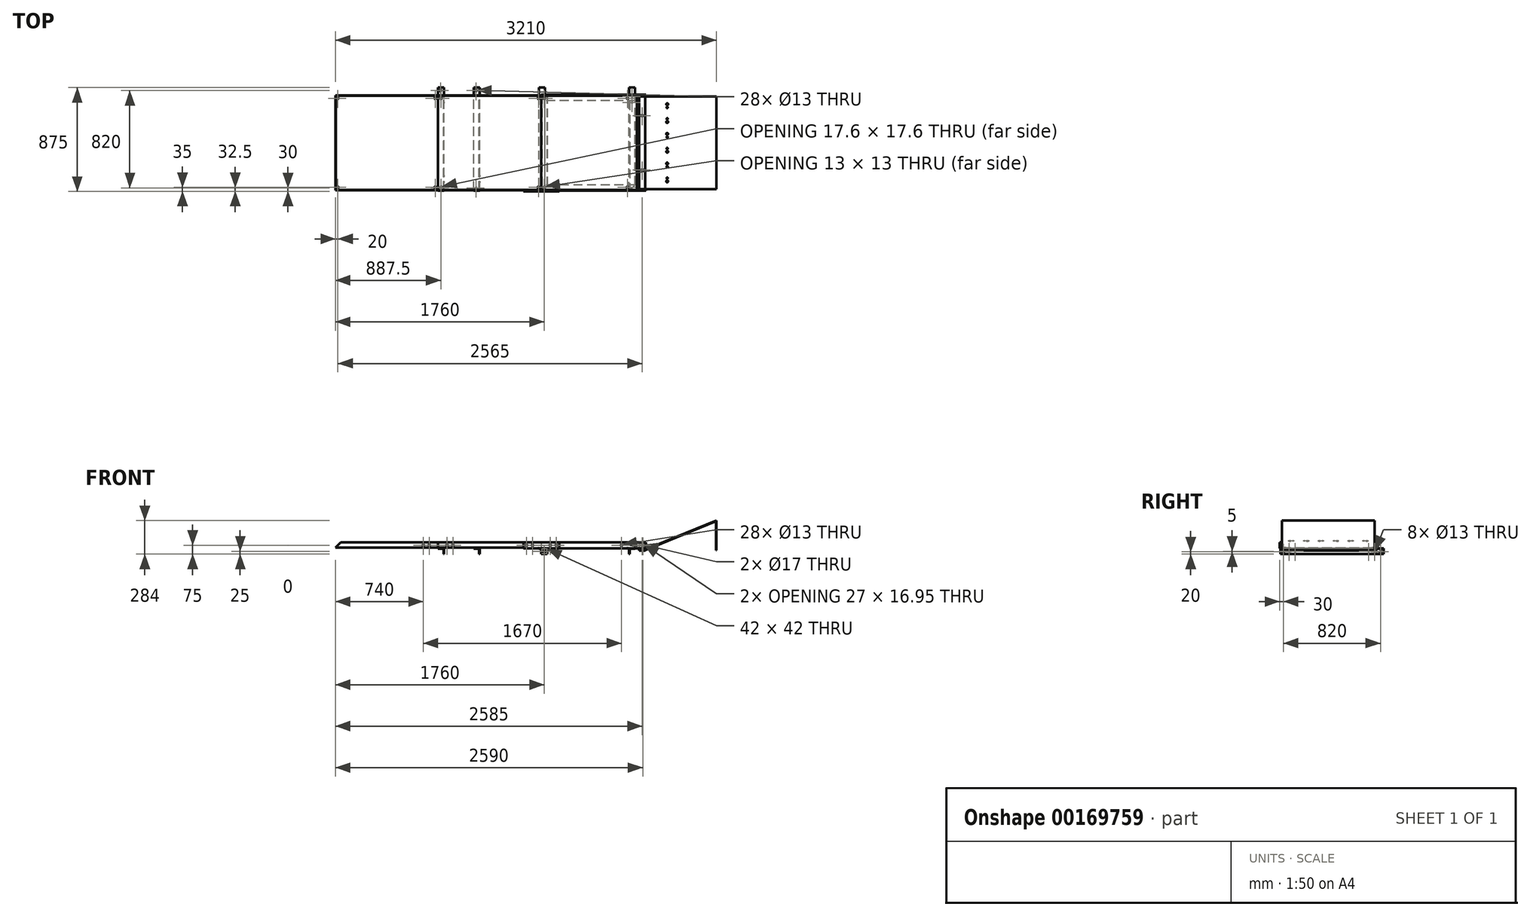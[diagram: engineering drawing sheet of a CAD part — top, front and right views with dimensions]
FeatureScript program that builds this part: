
annotation { "Feature Type Name" : "Feature", "Feature Type Description" : "" }
export const myFeature = defineFeature(function(context is Context, id is Id, definition is map)
    precondition{}
    {
        {
            var Q0;
            Q0=qCreatedBy(makeId("Front.planeOp"),FACE);
            var sketch = newSketch(context, id + "F0", { "sketchPlane" : qUnion([Q0])});
            skLineSegment(sketch, "E0", {"start": v(0, 0) * mm, "end": v(0, 4) * mm});
            skLineSegment(sketch, "E1", {"start": v(0, 4) * mm, "end": v(50, 4) * mm});
            skLineSegment(sketch, "E2", {"start": v(50, 4) * mm, "end": v(650, 250) * mm});
            skLineSegment(sketch, "E3", {"start": v(650, 250) * mm, "end": v(650, 0) * mm});
            skLineSegment(sketch, "E4", {"start": v(650, 0) * mm, "end": v(646, 0) * mm});
            skLineSegment(sketch, "E5", {"start": v(646, 0) * mm, "end": v(646, 244.04) * mm});
            skLineSegment(sketch, "E6", {"start": v(646, 244.04) * mm, "end": v(50.79, 0) * mm});
            skLineSegment(sketch, "E7", {"start": v(50.79, 0) * mm, "end": v(0, 0) * mm});
            skSolve(sketch);
        }
        {
            var Q0;
            Q0=qSketchRegion(id+"F0",true);
            extrude(context, id + "F1", {"entities" : qUnion([Q0]), "oppositeDirection" : true, "depth" : 780 * mm});
        }
        {
            var Q0;
            Q0=qCreatedBy(makeId("Right.planeOp"),FACE);
            var sketch = newSketch(context, id + "F2", { "sketchPlane" : qUnion([Q0])});
            skLineSegment(sketch, "E8", {"start": v(0, 0) * mm, "end": v(-7, 0) * mm});
            skLineSegment(sketch, "E9", {"start": v(-7, 0) * mm, "end": v(-7, 66) * mm});
            skLineSegment(sketch, "E10", {"start": v(-7, 66) * mm, "end": v(-11, 66) * mm});
            skLineSegment(sketch, "E11", {"start": v(-11, 66) * mm, "end": v(-11, -4) * mm});
            skLineSegment(sketch, "E12", {"start": v(-11, -4) * mm, "end": v(791, -4) * mm});
            skLineSegment(sketch, "E13", {"start": v(791, -4) * mm, "end": v(791, 66) * mm});
            skLineSegment(sketch, "E14", {"start": v(791, 66) * mm, "end": v(787, 66) * mm});
            skLineSegment(sketch, "E15", {"start": v(787, 66) * mm, "end": v(787, 0) * mm});
            skLineSegment(sketch, "E16", {"start": v(787, 0) * mm, "end": v(0, 0) * mm});
            skSolve(sketch);
        }
        {
            var Q0;
            Q0=makeQuery(id+"F2.imprint","IMPRINT",FACE,{"disambiguationData":[TD([[makeQuery(id+"F2.imprint","IMPRINT",EDGE,{"derivedFrom":sQuery(id+"F2.wireOp",EDGE,"E8")}),1.0]])]});
            extrude(context, id + "F3", {"entities" : qUnion([Q0]), "depth" : 50 * mm});
        }
        {
            var Q0;
            Q0=makeQuery(id+"F3.opExtrude","SWEPT_FACE",FACE,{"disambiguationData":[OSD([sQuery(id+"F2.wireOp",EDGE,"E11")])]});
            var sketch = newSketch(context, id + "F4", { "sketchPlane" : qUnion([Q0])});
            skCircle(sketch, "E17", {"center": v(20, 41) * mm, "radius": 8.5 * mm});
            skSolve(sketch);
        }
        {
            var Q0;
            Q0=qSketchRegion(id+"F4",true);
            extrude(context, id + "F5", {"entities" : qUnion([Q0]), "operationType" : NewBodyOperationType.REMOVE, "endBound" : BoundingType.THROUGH_ALL, "oppositeDirection" : true, "depth" : 25 * mm});
        }
        {
            var Q0;
            Q0=makeQuery(id+"F3.opExtrude","SWEPT_FACE",FACE,{"disambiguationData":[OSD([sQuery(id+"F2.wireOp",EDGE,"E11")])]});
            var sketch = newSketch(context, id + "F6", { "sketchPlane" : qUnion([Q0])});
            skLineSegment(sketch, "E18.bottom", {"start": v(55, 66) * mm, "end": v(-825, 66) * mm});
            skLineSegment(sketch, "E18.top", {"start": v(55, 16) * mm, "end": v(-825, 16) * mm});
            skLineSegment(sketch, "E18.left", {"start": v(55, 66) * mm, "end": v(55, 16) * mm});
            skLineSegment(sketch, "E18.right", {"start": v(-825, 66) * mm, "end": v(-825, 16) * mm});
            skSolve(sketch);
        }
        {
            var Q0;
            Q0=qSketchRegion(id+"F6",true);
            extrude(context, id + "F7", {"entities" : qUnion([Q0]), "depth" : 4 * mm});
        }
        {
            var Q0;
            Q0=makeQuery(id+"F7.opExtrude","CAP_FACE",FACE,{"disambiguationData":[OSD([sQuery(id+"F6.wireOp",EDGE,"E18.bottom"),sQuery(id+"F6.wireOp",EDGE,"E18.top"),sQuery(id+"F6.wireOp",EDGE,"E18.left"),sQuery(id+"F6.wireOp",EDGE,"E18.right")])],"isStart":true});
            var sketch = newSketch(context, id + "F8", { "sketchPlane" : qUnion([Q0])});
            skLineSegment(sketch, "E19.bottom", {"start": v(20, 16) * mm, "end": v(825, 16) * mm});
            skLineSegment(sketch, "E19.top", {"start": v(20, 20) * mm, "end": v(825, 20) * mm});
            skLineSegment(sketch, "E19.left", {"start": v(20, 16) * mm, "end": v(20, 20) * mm});
            skLineSegment(sketch, "E19.right", {"start": v(825, 16) * mm, "end": v(825, 20) * mm});
            skSolve(sketch);
        }
        {
            var Q0;
            Q0=qSketchRegion(id+"F8",true);
            extrude(context, id + "F9", {"entities" : qUnion([Q0]), "operationType" : NewBodyOperationType.ADD, "depth" : 46 * mm});
        }
        {
            var Q0;
            Q0=makeQuery(id+"F3.opExtrude","SWEPT_FACE",FACE,{"disambiguationData":[OSD([sQuery(id+"F2.wireOp",EDGE,"E13")])]});
            var sketch = newSketch(context, id + "F10", { "sketchPlane" : qUnion([Q0])});
            skLineSegment(sketch, "E20.bottom", {"start": v(-55, 66) * mm, "end": v(825, 66) * mm});
            skLineSegment(sketch, "E20.top", {"start": v(-55, 16) * mm, "end": v(825, 16) * mm});
            skLineSegment(sketch, "E20.left", {"start": v(-55, 66) * mm, "end": v(-55, 16) * mm});
            skLineSegment(sketch, "E20.right", {"start": v(825, 66) * mm, "end": v(825, 16) * mm});
            skSolve(sketch);
        }
        {
            var Q0;
            Q0=qSketchRegion(id+"F10",true);
            extrude(context, id + "F11", {"entities" : qUnion([Q0]), "depth" : 4 * mm});
        }
        {
            var Q0;
            Q0=makeQuery(id+"F11.opExtrude","CAP_FACE",FACE,{"disambiguationData":[OSD([sQuery(id+"F10.wireOp",EDGE,"E20.bottom"),sQuery(id+"F10.wireOp",EDGE,"E20.top"),sQuery(id+"F10.wireOp",EDGE,"E20.left"),sQuery(id+"F10.wireOp",EDGE,"E20.right")])],"isStart":true});
            var sketch = newSketch(context, id + "F12", { "sketchPlane" : qUnion([Q0])});
            skLineSegment(sketch, "E21.bottom", {"start": v(-825, 16) * mm, "end": v(-20, 16) * mm});
            skLineSegment(sketch, "E21.top", {"start": v(-825, 20) * mm, "end": v(-20, 20) * mm});
            skLineSegment(sketch, "E21.left", {"start": v(-825, 16) * mm, "end": v(-825, 20) * mm});
            skLineSegment(sketch, "E21.right", {"start": v(-20, 16) * mm, "end": v(-20, 20) * mm});
            skSolve(sketch);
        }
        {
            var Q0;
            Q0=makeQuery(id+"F12.imprint","IMPRINT",FACE,{"disambiguationData":[TD([[makeQuery(id+"F12.imprint","IMPRINT",EDGE,{"derivedFrom":sQuery(id+"F12.wireOp",EDGE,"E21.bottom")}),-1.0]])]});
            extrude(context, id + "F13", {"entities" : qUnion([Q0]), "operationType" : NewBodyOperationType.ADD, "depth" : 46 * mm});
        }
        {
            var Q0;
            Q0=makeQuery(id+"F9.boolean.opBoolean","MERGE",FACE,{"derivedFrom":[makeQuery(id+"F7.opExtrude","SWEPT_FACE",FACE,{"disambiguationData":[OSD([sQuery(id+"F6.wireOp",EDGE,"E18.top")])]}),makeQuery(id+"F9.opExtrude","SWEPT_FACE",FACE,{"disambiguationData":[OSD([sQuery(id+"F8.wireOp",EDGE,"E19.bottom")])]})]});
            var sketch = newSketch(context, id + "F14", { "sketchPlane" : qUnion([Q0])});
            skLineSegment(sketch, "E22.bottom", {"start": v(-845, 15) * mm, "end": v(-795, 15) * mm});
            skLineSegment(sketch, "E22.top", {"start": v(-845, -855) * mm, "end": v(-795, -855) * mm});
            skLineSegment(sketch, "E22.left", {"start": v(-845, 15) * mm, "end": v(-845, -855) * mm});
            skLineSegment(sketch, "E22.right", {"start": v(-795, 15) * mm, "end": v(-795, -855) * mm});
            skLineSegment(sketch, "E23.bottom", {"start": v(-1645, 15) * mm, "end": v(-1695, 15) * mm});
            skLineSegment(sketch, "E23.top", {"start": v(-1645, -855) * mm, "end": v(-1695, -855) * mm});
            skLineSegment(sketch, "E23.left", {"start": v(-1645, 15) * mm, "end": v(-1645, -855) * mm});
            skLineSegment(sketch, "E23.right", {"start": v(-1695, 15) * mm, "end": v(-1695, -855) * mm});
            skLineSegment(sketch, "E24.bottom", {"start": v(-35.12, 15) * mm, "end": v(-85.12, 15) * mm});
            skLineSegment(sketch, "E24.top", {"start": v(-35.12, -855) * mm, "end": v(-85.12, -855) * mm});
            skLineSegment(sketch, "E24.left", {"start": v(-35.12, 15) * mm, "end": v(-35.12, -855) * mm});
            skLineSegment(sketch, "E24.right", {"start": v(-85.12, 15) * mm, "end": v(-85.12, -855) * mm});
            skSolve(sketch);
        }
        {
            var Q0;
            Q0=qSketchRegion(id+"F14",true);
            extrude(context, id + "F15", {"entities" : qUnion([Q0]), "depth" : 4 * mm});
        }
        {
            var Q0;
            Q0=makeQuery(id+"F15.opExtrude","CAP_FACE",FACE,{"disambiguationData":[OSD([sQuery(id+"F14.wireOp",EDGE,"E23.bottom"),sQuery(id+"F14.wireOp",EDGE,"E23.top"),sQuery(id+"F14.wireOp",EDGE,"E23.left"),sQuery(id+"F14.wireOp",EDGE,"E23.right")])],"isStart":false});
            var sketch = newSketch(context, id + "F16", { "sketchPlane" : qUnion([Q0])});
            skLineSegment(sketch, "E25.bottom", {"start": v(-1645, 15) * mm, "end": v(-1649, 15) * mm});
            skLineSegment(sketch, "E25.top", {"start": v(-1645, -855) * mm, "end": v(-1649, -855) * mm});
            skLineSegment(sketch, "E25.left", {"start": v(-1645, 15) * mm, "end": v(-1645, -855) * mm});
            skLineSegment(sketch, "E25.right", {"start": v(-1649, 15) * mm, "end": v(-1649, -855) * mm});
            skSolve(sketch);
        }
        {
            var Q0;
            Q0=qSketchRegion(id+"F16",true);
            extrude(context, id + "F17", {"entities" : qUnion([Q0]), "operationType" : NewBodyOperationType.ADD, "depth" : 46 * mm});
        }
        {
            var Q0;
            Q0=makeQuery(id+"F15.opExtrude","CAP_FACE",FACE,{"disambiguationData":[OSD([sQuery(id+"F14.wireOp",EDGE,"E22.bottom"),sQuery(id+"F14.wireOp",EDGE,"E22.top"),sQuery(id+"F14.wireOp",EDGE,"E22.left"),sQuery(id+"F14.wireOp",EDGE,"E22.right")])],"isStart":false});
            var sketch = newSketch(context, id + "F18", { "sketchPlane" : qUnion([Q0])});
            skLineSegment(sketch, "E26.bottom", {"start": v(-795, -855) * mm, "end": v(-799, -855) * mm});
            skLineSegment(sketch, "E26.top", {"start": v(-795, 15) * mm, "end": v(-799, 15) * mm});
            skLineSegment(sketch, "E26.left", {"start": v(-795, -855) * mm, "end": v(-795, 15) * mm});
            skLineSegment(sketch, "E26.right", {"start": v(-799, -855) * mm, "end": v(-799, 15) * mm});
            skSolve(sketch);
        }
        {
            var Q0;
            Q0=qSketchRegion(id+"F18",true);
            extrude(context, id + "F19", {"entities" : qUnion([Q0]), "operationType" : NewBodyOperationType.ADD, "depth" : 44 * mm});
        }
        {
            var Q0;
            Q0=makeQuery(id+"F15.opExtrude","CAP_FACE",FACE,{"disambiguationData":[OSD([sQuery(id+"F14.wireOp",EDGE,"E24.bottom"),sQuery(id+"F14.wireOp",EDGE,"E24.top"),sQuery(id+"F14.wireOp",EDGE,"E24.left"),sQuery(id+"F14.wireOp",EDGE,"E24.right")])],"isStart":false});
            var sketch = newSketch(context, id + "F20", { "sketchPlane" : qUnion([Q0])});
            skLineSegment(sketch, "E27.bottom", {"start": v(-85.12, -855) * mm, "end": v(-81.12, -855) * mm});
            skLineSegment(sketch, "E27.top", {"start": v(-85.12, 15) * mm, "end": v(-81.12, 15) * mm});
            skLineSegment(sketch, "E27.left", {"start": v(-85.12, -855) * mm, "end": v(-85.12, 15) * mm});
            skLineSegment(sketch, "E27.right", {"start": v(-81.12, -855) * mm, "end": v(-81.12, 15) * mm});
            skSolve(sketch);
        }
        {
            var Q0;
            Q0=qSketchRegion(id+"F20",true);
            extrude(context, id + "F21", {"entities" : qUnion([Q0]), "operationType" : NewBodyOperationType.ADD, "depth" : 46 * mm});
        }
        {
            var Q0;
            Q0=makeQuery(id+"F7.opExtrude","CAP_FACE",FACE,{"disambiguationData":[OSD([sQuery(id+"F6.wireOp",EDGE,"E18.bottom"),sQuery(id+"F6.wireOp",EDGE,"E18.top"),sQuery(id+"F6.wireOp",EDGE,"E18.left"),sQuery(id+"F6.wireOp",EDGE,"E18.right")])],"isStart":false});
            var sketch = newSketch(context, id + "F22", { "sketchPlane" : qUnion([Q0])});
            skCircle(sketch, "E28", {"center": v(30, 41) * mm, "radius": 8.5 * mm});
            skPoint(sketch, "E28.centerSnap0", {"position": v(55, 41) * mm});
            skSolve(sketch);
        }
        {
            var Q0;
            Q0=qSketchRegion(id+"F22",true);
            extrude(context, id + "F23", {"entities" : qUnion([Q0]), "operationType" : NewBodyOperationType.REMOVE, "endBound" : BoundingType.THROUGH_ALL, "oppositeDirection" : true, "depth" : 25 * mm});
        }
        {
            var Q0;
            Q0=makeQuery(id+"F11.opExtrude","CAP_FACE",FACE,{"disambiguationData":[OSD([sQuery(id+"F10.wireOp",EDGE,"E20.bottom"),sQuery(id+"F10.wireOp",EDGE,"E20.top"),sQuery(id+"F10.wireOp",EDGE,"E20.left"),sQuery(id+"F10.wireOp",EDGE,"E20.right")])],"isStart":false});
            var sketch = newSketch(context, id + "F24", { "sketchPlane" : qUnion([Q0])});
            skSolve(sketch);
        }
        {
            var Q0;
            Q0=makeQuery(id+"F11.opExtrude","CAP_FACE",FACE,{"disambiguationData":[OSD([sQuery(id+"F10.wireOp",EDGE,"E20.bottom"),sQuery(id+"F10.wireOp",EDGE,"E20.top"),sQuery(id+"F10.wireOp",EDGE,"E20.left"),sQuery(id+"F10.wireOp",EDGE,"E20.right")])],"isStart":true});
            var sketch = newSketch(context, id + "F25", { "sketchPlane" : qUnion([Q0])});
            skCircle(sketch, "E29", {"center": v(30, 41) * mm, "radius": 8.5 * mm});
            skPoint(sketch, "E29.centerSnap0", {"position": v(55, 41) * mm});
            skSolve(sketch);
        }
        {
            var Q0;
            Q0=qSketchRegion(id+"F25",true);
            extrude(context, id + "F26", {"entities" : qUnion([Q0]), "operationType" : NewBodyOperationType.REMOVE, "endBound" : BoundingType.THROUGH_ALL, "oppositeDirection" : true, "depth" : 25 * mm});
        }
        {
            var Q0;
            Q0=makeQuery(id+"F1.opExtrude","SWEPT_FACE",FACE,{"disambiguationData":[OSD([sQuery(id+"F0.wireOp",EDGE,"E2")])]});
            var sketch = newSketch(context, id + "F27", { "sketchPlane" : qUnion([Q0])});
            skCircle(sketch, "E30", {"center": v(247.78, 715) * mm, "radius": 8.5 * mm});
            skCircle(sketch, "E31", {"center": v(247.78, 565) * mm, "radius": 8.5 * mm});
            skCircle(sketch, "E32", {"center": v(247.78, 465) * mm, "radius": 8.5 * mm});
            skCircle(sketch, "E33", {"center": v(247.78, 315) * mm, "radius": 8.5 * mm});
            skCircle(sketch, "E34", {"center": v(247.78, 215) * mm, "radius": 8.5 * mm});
            skCircle(sketch, "E35", {"center": v(247.78, 65) * mm, "radius": 8.5 * mm});
            skCircle(sketch, "E36", {"center": v(247.78, 688) * mm, "radius": 5.75 * mm});
            skCircle(sketch, "E37", {"center": v(247.78, 592) * mm, "radius": 5.75 * mm});
            skCircle(sketch, "E38", {"center": v(247.78, 438) * mm, "radius": 5.75 * mm});
            skCircle(sketch, "E39", {"center": v(247.78, 342) * mm, "radius": 5.75 * mm});
            skCircle(sketch, "E40", {"center": v(247.78, 188) * mm, "radius": 5.75 * mm});
            skCircle(sketch, "E41", {"center": v(247.78, 92) * mm, "radius": 5.75 * mm});
            skSolve(sketch);
        }
        {
            var Q0;
            Q0=qSketchRegion(id+"F27",true);
            extrude(context, id + "F28", {"entities" : qUnion([Q0]), "operationType" : NewBodyOperationType.REMOVE, "endBound" : BoundingType.THROUGH_ALL, "oppositeDirection" : true, "depth" : 25 * mm});
        }
        {
            var Q0;
            Q0=makeQuery(id+"F3.opExtrude","SWEPT_FACE",FACE,{"disambiguationData":[OSD([sQuery(id+"F2.wireOp",EDGE,"E12")])]});
            var sketch = newSketch(context, id + "F29", { "sketchPlane" : qUnion([Q0])});
            skCircle(sketch, "E42", {"center": v(25, -619) * mm, "radius": 6 * mm});
            skPoint(sketch, "E42.centerSnap0", {"position": v(25, -791) * mm});
            skCircle(sketch, "E43", {"center": v(25, -161) * mm, "radius": 6 * mm});
            skPoint(sketch, "E43.centerSnap0", {"position": v(25, 11) * mm});
            skLineSegment(sketch, "E44", {"start": v(50, -390) * mm, "end": v(0, -390) * mm});
            skSolve(sketch);
        }
        {
            var Q0;
            Q0=qSketchRegion(id+"F29",true);
            extrude(context, id + "F30", {"entities" : qUnion([Q0]), "operationType" : NewBodyOperationType.REMOVE, "endBound" : BoundingType.THROUGH_ALL, "oppositeDirection" : true, "depth" : 25 * mm});
        }
        {
            var Q0;
            Q0=makeQuery(id+"F1.opExtrude","SWEPT_FACE",FACE,{"disambiguationData":[OSD([sQuery(id+"F0.wireOp",EDGE,"E1")])]});
            var sketch = newSketch(context, id + "F31", { "sketchPlane" : qUnion([Q0])});
            skCircle(sketch, "E45", {"center": v(25, 619) * mm, "radius": 6.5 * mm});
            skPoint(sketch, "E45.centerSnap0", {"position": v(25, 780) * mm});
            skCircle(sketch, "E46", {"center": v(25, 161) * mm, "radius": 6.5 * mm});
            skLineSegment(sketch, "E47", {"start": v(50, 390) * mm, "end": v(0, 390) * mm});
            skSolve(sketch);
        }
        {
            var Q0;
            Q0=qSketchRegion(id+"F31",true);
            extrude(context, id + "F32", {"entities" : qUnion([Q0]), "operationType" : NewBodyOperationType.REMOVE, "endBound" : BoundingType.THROUGH_ALL, "oppositeDirection" : true, "depth" : 25 * mm});
        }
        {
            var Q0;
            Q0=makeQuery(id+"F7.opExtrude","CAP_FACE",FACE,{"disambiguationData":[OSD([sQuery(id+"F6.wireOp",EDGE,"E18.bottom"),sQuery(id+"F6.wireOp",EDGE,"E18.top"),sQuery(id+"F6.wireOp",EDGE,"E18.left"),sQuery(id+"F6.wireOp",EDGE,"E18.right")])],"isStart":false});
            var sketch = newSketch(context, id + "F33", { "sketchPlane" : qUnion([Q0])});
            skLineSegment(sketch, "E48.bottom", {"start": v(-825, 16) * mm, "end": v(-775, 16) * mm});
            skLineSegment(sketch, "E48.top", {"start": v(-825, -34) * mm, "end": v(-775, -34) * mm});
            skLineSegment(sketch, "E48.left", {"start": v(-825, 16) * mm, "end": v(-825, -34) * mm});
            skLineSegment(sketch, "E48.right", {"start": v(-775, 16) * mm, "end": v(-775, -34) * mm});
            skLineSegment(sketch, "E49.0", {"start": v(-779, 12) * mm, "end": v(-779, -30) * mm});
            skLineSegment(sketch, "E49.1", {"start": v(-821, 12) * mm, "end": v(-779, 12) * mm});
            skLineSegment(sketch, "E49.2", {"start": v(-821, 12) * mm, "end": v(-821, -30) * mm});
            skLineSegment(sketch, "E49.3", {"start": v(-821, -30) * mm, "end": v(-779, -30) * mm});
            skSolve(sketch);
        }
        {
            var Q0;
            Q0=makeQuery(id+"F33.imprint","IMPRINT",FACE,{"disambiguationData":[TD([[makeQuery(id+"F33.imprint","IMPRINT",EDGE,{"derivedFrom":sQuery(id+"F33.wireOp",EDGE,"E48.bottom")}),1.0]])]});
            extrude(context, id + "F34", {"entities" : qUnion([Q0]), "oppositeDirection" : true, "depth" : 810 * mm});
        }
        {
            var Q0;
            Q0=makeQuery(id+"F15.opExtrude","SWEPT_BODY",BODY,{"disambiguationData":[OSD([sQuery(id+"F14.wireOp",EDGE,"E23.bottom"),sQuery(id+"F14.wireOp",EDGE,"E23.top"),sQuery(id+"F14.wireOp",EDGE,"E23.left"),sQuery(id+"F14.wireOp",EDGE,"E23.right")])]});
            transform(context, id + "F35", {"entities" : qUnion([Q0]), "transformType" : TransformType.TRANSLATION_3D, "dx" : 300 * mm, "dy" : 0 * mm, "dz" : 0 * mm, "makeCopy" : true});
        }
        {
            var Q0;
            Q0=makeQuery(id+"F7.opExtrude","CAP_FACE",FACE,{"disambiguationData":[OSD([sQuery(id+"F6.wireOp",EDGE,"E18.bottom"),sQuery(id+"F6.wireOp",EDGE,"E18.top"),sQuery(id+"F6.wireOp",EDGE,"E18.left"),sQuery(id+"F6.wireOp",EDGE,"E18.right")])],"isStart":false});
            var sketch = newSketch(context, id + "F36", { "sketchPlane" : qUnion([Q0])});
            skLineSegment(sketch, "E50.bottom", {"start": v(-675, 16) * mm, "end": v(-975, 16) * mm});
            skLineSegment(sketch, "E50.top", {"start": v(-675, 66) * mm, "end": v(-975, 66) * mm});
            skLineSegment(sketch, "E50.left", {"start": v(-675, 16) * mm, "end": v(-675, 66) * mm});
            skLineSegment(sketch, "E50.right", {"start": v(-975, 16) * mm, "end": v(-975, 66) * mm});
            skCircle(sketch, "E51", {"center": v(-700, 41) * mm, "radius": 6.5 * mm});
            skPoint(sketch, "E51.centerSnap0", {"position": v(-675, 41) * mm});
            skCircle(sketch, "E52", {"center": v(-750, 41) * mm, "radius": 6.5 * mm});
            skCircle(sketch, "E53", {"center": v(-900, 41) * mm, "radius": 6.5 * mm});
            skCircle(sketch, "E54", {"center": v(-950, 41) * mm, "radius": 6.5 * mm});
            skSolve(sketch);
        }
        {
            var Q0;
            Q0=qSketchRegion(id+"F36",true);
            var Q1;
            {var subQ2=sQuery(id+"F36.wireOp",EDGE,"E50.right");Q1=makeQuery(id+"F36.imprint","IMPRINT",FACE,{"disambiguationData":[TD([[makeQuery(id+"F36.imprint","IMPRINT",EDGE,{"derivedFrom":subQ2}),-1.0]])]});}
            extrude(context, id + "F37", {"entities" : qUnion([Q0, Q1]), "depth" : 5 * mm});
        }
        {
            var Q0;
            Q0=makeQuery(id+"F7.opExtrude","CAP_FACE",FACE,{"disambiguationData":[OSD([sQuery(id+"F6.wireOp",EDGE,"E18.bottom"),sQuery(id+"F6.wireOp",EDGE,"E18.top"),sQuery(id+"F6.wireOp",EDGE,"E18.left"),sQuery(id+"F6.wireOp",EDGE,"E18.right")])],"isStart":false});
            var sketch = newSketch(context, id + "F38", { "sketchPlane" : qUnion([Q0])});
            skCircle(sketch, "E55", {"center": v(-750, 41) * mm, "radius": 6.5 * mm});
            skPoint(sketch, "E55.centerSnap0", {"position": v(-825, 41) * mm});
            skCircle(sketch, "E56", {"center": v(-700, 41) * mm, "radius": 6.5 * mm});
            skSolve(sketch);
        }
        {
            var Q0;
            Q0=makeQuery(id+"F38.imprint","IMPRINT",FACE,{"disambiguationData":[TD([[makeQuery(id+"F38.imprint","IMPRINT",EDGE,{"derivedFrom":sQuery(id+"F38.wireOp",EDGE,"E55")}),1.0]])]});
            var Q1;
            Q1=makeQuery(id+"F38.imprint","IMPRINT",FACE,{"disambiguationData":[TD([[makeQuery(id+"F38.imprint","IMPRINT",EDGE,{"derivedFrom":sQuery(id+"F38.wireOp",EDGE,"E56")}),1.0]])]});
            extrude(context, id + "F39", {"entities" : qUnion([Q0, Q1]), "operationType" : NewBodyOperationType.REMOVE, "endBound" : BoundingType.THROUGH_ALL, "oppositeDirection" : true, "depth" : 25 * mm});
        }
        {
            var Q0;
            Q0=makeQuery(id+"F24.imprint","IMPRINT",FACE,{"disambiguationData":[TD([[makeQuery(id+"F24.imprint","IMPRINT",EDGE,{"derivedFrom":makeQuery(id+"F11.opExtrude","CAP_EDGE",EDGE,{"disambiguationData":[OSD([sQuery(id+"F10.wireOp",EDGE,"E20.bottom")])],"isStart":false})}),-1.0]])]});
            var sketch = newSketch(context, id + "F40", { "sketchPlane" : qUnion([Q0])});
            skCircle(sketch, "E57", {"center": v(750, 41) * mm, "radius": 6.5 * mm});
            skCircle(sketch, "E58", {"center": v(700, 41) * mm, "radius": 6.5 * mm});
            skSolve(sketch);
        }
        {
            var Q0;
            Q0=makeQuery(id+"F40.imprint","IMPRINT",FACE,{"disambiguationData":[TD([[makeQuery(id+"F40.imprint","IMPRINT",EDGE,{"derivedFrom":sQuery(id+"F40.wireOp",EDGE,"E58")}),1.0]])]});
            var Q1;
            Q1=makeQuery(id+"F40.imprint","IMPRINT",FACE,{"disambiguationData":[TD([[makeQuery(id+"F40.imprint","IMPRINT",EDGE,{"derivedFrom":sQuery(id+"F40.wireOp",EDGE,"E57")}),1.0]])]});
            extrude(context, id + "F41", {"entities" : qUnion([Q0, Q1]), "operationType" : NewBodyOperationType.REMOVE, "endBound" : BoundingType.THROUGH_ALL, "oppositeDirection" : true, "depth" : 25 * mm});
        }
        {
            var Q0;
            Q0=makeQuery(id+"F17.boolean.opBoolean","MERGE",FACE,{"derivedFrom":[makeQuery(id+"F15.opExtrude","SWEPT_FACE",FACE,{"disambiguationData":[OSD([sQuery(id+"F14.wireOp",EDGE,"E23.left")])]}),makeQuery(id+"F17.opExtrude","SWEPT_FACE",FACE,{"disambiguationData":[OSD([sQuery(id+"F16.wireOp",EDGE,"E25.left")])]})]});
            var sketch = newSketch(context, id + "F42", { "sketchPlane" : qUnion([Q0])});
            skCircle(sketch, "E59", {"center": v(60, -9) * mm, "radius": 6.5 * mm});
            skPoint(sketch, "E59.centerSnap0", {"position": v(-15, -9) * mm});
            skPoint(sketch, "E59.perimeterSnap0", {"position": v(-15, -9) * mm});
            skCircle(sketch, "E60", {"center": v(110, -9) * mm, "radius": 6.5 * mm});
            skCircle(sketch, "E61", {"center": v(780, -9) * mm, "radius": 6.5 * mm});
            skPoint(sketch, "E61.centerSnap0", {"position": v(855, -9) * mm});
            skCircle(sketch, "E62", {"center": v(730, -9) * mm, "radius": 6.5 * mm});
            skSolve(sketch);
        }
        {
            var Q0;
            Q0=qSketchRegion(id+"F42",true);
            extrude(context, id + "F43", {"entities" : qUnion([Q0]), "operationType" : NewBodyOperationType.REMOVE, "oppositeDirection" : true, "depth" : 25 * mm});
        }
        {
            var Q0;
            Q0=makeQuery(id+"F35.opPattern","COPY",FACE,{"derivedFrom":makeQuery(id+"F17.boolean.opBoolean","MERGE",FACE,{"derivedFrom":[makeQuery(id+"F15.opExtrude","SWEPT_FACE",FACE,{"disambiguationData":[OSD([sQuery(id+"F14.wireOp",EDGE,"E23.left")])]}),makeQuery(id+"F17.opExtrude","SWEPT_FACE",FACE,{"disambiguationData":[OSD([sQuery(id+"F16.wireOp",EDGE,"E25.left")])]})]}),"instanceName":"1"});
            var sketch = newSketch(context, id + "F44", { "sketchPlane" : qUnion([Q0])});
            skCircle(sketch, "E63", {"center": v(60, -9) * mm, "radius": 6.5 * mm});
            skPoint(sketch, "E63.centerSnap0", {"position": v(-15, -9) * mm});
            skCircle(sketch, "E64", {"center": v(110, -9) * mm, "radius": 6.5 * mm});
            skSolve(sketch);
        }
        {
            var Q0;
            Q0=makeQuery(id+"F44.imprint","IMPRINT",FACE,{"disambiguationData":[TD([[makeQuery(id+"F44.imprint","IMPRINT",EDGE,{"derivedFrom":sQuery(id+"F44.wireOp",EDGE,"E63")}),1.0]])]});
            var Q1;
            Q1=makeQuery(id+"F44.imprint","IMPRINT",FACE,{"disambiguationData":[TD([[makeQuery(id+"F44.imprint","IMPRINT",EDGE,{"derivedFrom":sQuery(id+"F44.wireOp",EDGE,"E64")}),1.0]])]});
            extrude(context, id + "F45", {"entities" : qUnion([Q0, Q1]), "operationType" : NewBodyOperationType.REMOVE, "endBound" : BoundingType.THROUGH_ALL, "oppositeDirection" : true, "depth" : 25 * mm});
        }
        {
            var Q0;
            Q0=makeQuery(id+"F35.opPattern","COPY",BODY,{"derivedFrom":makeQuery(id+"F15.opExtrude","SWEPT_BODY",BODY,{"disambiguationData":[OSD([sQuery(id+"F14.wireOp",EDGE,"E23.bottom"),sQuery(id+"F14.wireOp",EDGE,"E23.top"),sQuery(id+"F14.wireOp",EDGE,"E23.left"),sQuery(id+"F14.wireOp",EDGE,"E23.right")])]}),"instanceName":"1"});
            transform(context, id + "F46", {"entities" : qUnion([Q0]), "transformType" : TransformType.TRANSLATION_3D, "dx" : 150 * mm, "dy" : 0 * mm, "dz" : 0 * mm, "makeCopy" : true});
        }
        {
            var Q0;
            Q0=makeQuery(id+"F35.opPattern","COPY",BODY,{"derivedFrom":makeQuery(id+"F15.opExtrude","SWEPT_BODY",BODY,{"disambiguationData":[OSD([sQuery(id+"F14.wireOp",EDGE,"E23.bottom"),sQuery(id+"F14.wireOp",EDGE,"E23.top"),sQuery(id+"F14.wireOp",EDGE,"E23.left"),sQuery(id+"F14.wireOp",EDGE,"E23.right")])]}),"instanceName":"1"});
            transform(context, id + "F47", {"entities" : qUnion([Q0]), "transformType" : TransformType.TRANSLATION_3D, "dx" : 250 * mm, "dy" : 0 * mm, "dz" : 0 * mm, "makeCopy" : true});
        }
        {
            var Q0;
            Q0=makeQuery(id+"F47.opPattern","COPY",BODY,{"derivedFrom":makeQuery(id+"F35.opPattern","COPY",BODY,{"derivedFrom":makeQuery(id+"F15.opExtrude","SWEPT_BODY",BODY,{"disambiguationData":[OSD([sQuery(id+"F14.wireOp",EDGE,"E23.bottom"),sQuery(id+"F14.wireOp",EDGE,"E23.top"),sQuery(id+"F14.wireOp",EDGE,"E23.left"),sQuery(id+"F14.wireOp",EDGE,"E23.right")])]}),"instanceName":"1"}),"instanceName":"1"});
            deleteBodies(context, id + "F48", {"entities" : qUnion([Q0])});
        }
        {
            var Q0;
            Q0=makeQuery(id+"F46.opPattern","COPY",BODY,{"derivedFrom":makeQuery(id+"F35.opPattern","COPY",BODY,{"derivedFrom":makeQuery(id+"F15.opExtrude","SWEPT_BODY",BODY,{"disambiguationData":[OSD([sQuery(id+"F14.wireOp",EDGE,"E23.bottom"),sQuery(id+"F14.wireOp",EDGE,"E23.top"),sQuery(id+"F14.wireOp",EDGE,"E23.left"),sQuery(id+"F14.wireOp",EDGE,"E23.right")])]}),"instanceName":"1"}),"instanceName":"1"});
            deleteBodies(context, id + "F49", {"entities" : qUnion([Q0])});
        }
        {
            var Q0;
            Q0=makeQuery(id+"F15.opExtrude","CAP_FACE",FACE,{"disambiguationData":[OSD([sQuery(id+"F14.wireOp",EDGE,"E24.bottom"),sQuery(id+"F14.wireOp",EDGE,"E24.top"),sQuery(id+"F14.wireOp",EDGE,"E24.left"),sQuery(id+"F14.wireOp",EDGE,"E24.right")])],"isStart":true});
            var sketch = newSketch(context, id + "F50", { "sketchPlane" : qUnion([Q0])});
            skCircle(sketch, "E65", {"center": v(-60.12, 780) * mm, "radius": 6.5 * mm});
            skCircle(sketch, "E66", {"center": v(-60.12, 730) * mm, "radius": 6.5 * mm});
            skSolve(sketch);
        }
        {
            var Q0;
            Q0=qSketchRegion(id+"F50",true);
            extrude(context, id + "F51", {"entities" : qUnion([Q0]), "operationType" : NewBodyOperationType.REMOVE, "oppositeDirection" : true, "depth" : 25 * mm});
        }
        {
            var Q0;
            Q0=makeQuery(id+"F34.opExtrude","SWEPT_FACE",FACE,{"disambiguationData":[OSD([sQuery(id+"F33.wireOp",EDGE,"E48.bottom")])]});
            var sketch = newSketch(context, id + "F52", { "sketchPlane" : qUnion([Q0])});
            skCircle(sketch, "E67", {"center": v(-800, 15) * mm, "radius": 6.5 * mm});
            skPoint(sketch, "E67.centerSnap0", {"position": v(-800, -15) * mm});
            skCircle(sketch, "E68", {"center": v(-800, 765) * mm, "radius": 6.5 * mm});
            skSolve(sketch);
        }
        {
            var Q0;
            Q0=makeQuery(id+"F35.opPattern","COPY",FACE,{"derivedFrom":makeQuery(id+"F17.boolean.opBoolean","MERGE",FACE,{"derivedFrom":[makeQuery(id+"F15.opExtrude","SWEPT_FACE",FACE,{"disambiguationData":[OSD([sQuery(id+"F14.wireOp",EDGE,"E23.left")])]}),makeQuery(id+"F17.opExtrude","SWEPT_FACE",FACE,{"disambiguationData":[OSD([sQuery(id+"F16.wireOp",EDGE,"E25.left")])]})]}),"instanceName":"1"});
            var sketch = newSketch(context, id + "F53", { "sketchPlane" : qUnion([Q0])});
            skLineSegment(sketch, "E69", {"start": v(855, 16) * mm, "end": v(805, -34) * mm});
            skLineSegment(sketch, "E70", {"start": v(805, -34) * mm, "end": v(855, -34) * mm});
            skLineSegment(sketch, "E71", {"start": v(855, -34) * mm, "end": v(855, 16) * mm});
            skSolve(sketch);
        }
        {
            var Q0;
            Q0=qSketchRegion(id+"F53",true);
            extrude(context, id + "F54", {"entities" : qUnion([Q0]), "operationType" : NewBodyOperationType.REMOVE, "endBound" : BoundingType.THROUGH_ALL, "oppositeDirection" : true, "depth" : 25 * mm});
        }
        {
            var Q0;
            Q0=makeQuery(id+"F15.opExtrude","CAP_FACE",FACE,{"disambiguationData":[OSD([sQuery(id+"F14.wireOp",EDGE,"E24.bottom"),sQuery(id+"F14.wireOp",EDGE,"E24.top"),sQuery(id+"F14.wireOp",EDGE,"E24.left"),sQuery(id+"F14.wireOp",EDGE,"E24.right")])],"isStart":true});
            var sketch = newSketch(context, id + "F55", { "sketchPlane" : qUnion([Q0])});
            skSolve(sketch);
        }
        {
            var Q0;
            Q0=makeQuery(id+"F55.imprint","IMPRINT",FACE,{"disambiguationData":[TD([[makeQuery(id+"F55.imprint","IMPRINT",EDGE,{"derivedFrom":makeQuery(id+"F15.opExtrude","CAP_EDGE",EDGE,{"disambiguationData":[OSD([sQuery(id+"F14.wireOp",EDGE,"E24.bottom")])],"isStart":true})}),-1.0]])]});
            var sketch = newSketch(context, id + "F56", { "sketchPlane" : qUnion([Q0])});
            skLineSegment(sketch, "E72", {"start": v(-35.12, 35) * mm, "end": v(-85.12, -15) * mm});
            skLineSegment(sketch, "E73", {"start": v(-85.12, -15) * mm, "end": v(-35.12, -15) * mm});
            skLineSegment(sketch, "E74", {"start": v(-35.12, -15) * mm, "end": v(-35.12, 35) * mm});
            skSolve(sketch);
        }
        {
            var Q0;
            Q0=makeQuery(id+"F56.imprint","IMPRINT",FACE,{"disambiguationData":[TD([[makeQuery(id+"F56.imprint","IMPRINT",EDGE,{"derivedFrom":sQuery(id+"F56.wireOp",EDGE,"E72")}),1.0]])]});
            extrude(context, id + "F57", {"entities" : qUnion([Q0]), "operationType" : NewBodyOperationType.REMOVE, "endBound" : BoundingType.THROUGH_ALL, "oppositeDirection" : true, "depth" : 25 * mm});
        }
        {
            var Q0;
            Q0=makeQuery(id+"F52.imprint","IMPRINT",FACE,{"disambiguationData":[TD([[makeQuery(id+"F52.imprint","IMPRINT",EDGE,{"derivedFrom":sQuery(id+"F52.wireOp",EDGE,"E68")}),1.0]])]});
            var Q1;
            Q1=makeQuery(id+"F52.imprint","IMPRINT",FACE,{"disambiguationData":[TD([[makeQuery(id+"F52.imprint","IMPRINT",EDGE,{"derivedFrom":sQuery(id+"F52.wireOp",EDGE,"E67")}),1.0]])]});
            extrude(context, id + "F58", {"entities" : qUnion([Q0, Q1]), "operationType" : NewBodyOperationType.REMOVE, "oppositeDirection" : true, "depth" : 25 * mm});
        }
        {
            var Q0;
            Q0=makeQuery(id+"F9.opExtrude","SWEPT_FACE",FACE,{"disambiguationData":[OSD([sQuery(id+"F8.wireOp",EDGE,"E19.top")])]});
            var sketch = newSketch(context, id + "F59", { "sketchPlane" : qUnion([Q0])});
            skCircle(sketch, "E75", {"center": v(-800, 15) * mm, "radius": 6.5 * mm});
            skCircle(sketch, "E76", {"center": v(-100, 15) * mm, "radius": 6.5 * mm});
            skSolve(sketch);
        }
        {
            var Q0;
            Q0=makeQuery(id+"F59.imprint","IMPRINT",FACE,{"disambiguationData":[TD([[makeQuery(id+"F59.imprint","IMPRINT",EDGE,{"derivedFrom":sQuery(id+"F59.wireOp",EDGE,"E76")}),1.0]])]});
            var Q1;
            Q1=makeQuery(id+"F59.imprint","IMPRINT",FACE,{"disambiguationData":[TD([[makeQuery(id+"F59.imprint","IMPRINT",EDGE,{"derivedFrom":sQuery(id+"F59.wireOp",EDGE,"E75")}),1.0]])]});
            extrude(context, id + "F60", {"entities" : qUnion([Q0, Q1]), "operationType" : NewBodyOperationType.REMOVE, "oppositeDirection" : true, "depth" : 25 * mm});
        }
        {
            var Q0;
            Q0=makeQuery(id+"F13.opExtrude","SWEPT_FACE",FACE,{"disambiguationData":[OSD([sQuery(id+"F12.wireOp",EDGE,"E21.top")])]});
            var sketch = newSketch(context, id + "F61", { "sketchPlane" : qUnion([Q0])});
            skCircle(sketch, "E77", {"center": v(-800, 765) * mm, "radius": 6.5 * mm});
            skCircle(sketch, "E78", {"center": v(-100, 765) * mm, "radius": 6.5 * mm});
            skSolve(sketch);
        }
        {
            var Q0;
            Q0=makeQuery(id+"F61.imprint","IMPRINT",FACE,{"disambiguationData":[TD([[makeQuery(id+"F61.imprint","IMPRINT",EDGE,{"derivedFrom":sQuery(id+"F61.wireOp",EDGE,"E78")}),1.0]])]});
            var Q1;
            Q1=makeQuery(id+"F61.imprint","IMPRINT",FACE,{"disambiguationData":[TD([[makeQuery(id+"F61.imprint","IMPRINT",EDGE,{"derivedFrom":sQuery(id+"F61.wireOp",EDGE,"E77")}),1.0]])]});
            extrude(context, id + "F62", {"entities" : qUnion([Q0, Q1]), "operationType" : NewBodyOperationType.REMOVE, "oppositeDirection" : true, "depth" : 25 * mm});
        }
        {
            var Q0;
            Q0=makeQuery(id+"F15.opExtrude","CAP_FACE",FACE,{"disambiguationData":[OSD([sQuery(id+"F14.wireOp",EDGE,"E23.bottom"),sQuery(id+"F14.wireOp",EDGE,"E23.top"),sQuery(id+"F14.wireOp",EDGE,"E23.left"),sQuery(id+"F14.wireOp",EDGE,"E23.right")])],"isStart":false});
            var sketch = newSketch(context, id + "F63", { "sketchPlane" : qUnion([Q0])});
            skCircle(sketch, "E79", {"center": v(-1675, -830) * mm, "radius": 6.5 * mm});
            skCircle(sketch, "E80", {"center": v(-1675, -10) * mm, "radius": 6.5 * mm});
            skSolve(sketch);
        }
        {
            var Q0;
            Q0=makeQuery(id+"F63.imprint","IMPRINT",FACE,{"disambiguationData":[TD([[makeQuery(id+"F63.imprint","IMPRINT",EDGE,{"derivedFrom":sQuery(id+"F63.wireOp",EDGE,"E79")}),1.0]])]});
            var Q1;
            Q1=makeQuery(id+"F63.imprint","IMPRINT",FACE,{"disambiguationData":[TD([[makeQuery(id+"F63.imprint","IMPRINT",EDGE,{"derivedFrom":sQuery(id+"F63.wireOp",EDGE,"E80")}),1.0]])]});
            extrude(context, id + "F64", {"entities" : qUnion([Q0, Q1]), "operationType" : NewBodyOperationType.REMOVE, "oppositeDirection" : true, "depth" : 25 * mm});
        }
        {
            var Q0;
            Q0=makeQuery(id+"F35.opPattern","COPY",FACE,{"derivedFrom":makeQuery(id+"F15.opExtrude","CAP_FACE",FACE,{"disambiguationData":[OSD([sQuery(id+"F14.wireOp",EDGE,"E23.bottom"),sQuery(id+"F14.wireOp",EDGE,"E23.top"),sQuery(id+"F14.wireOp",EDGE,"E23.left"),sQuery(id+"F14.wireOp",EDGE,"E23.right")])],"isStart":false}),"instanceName":"1"});
            var sketch = newSketch(context, id + "F65", { "sketchPlane" : qUnion([Q0])});
            skCircle(sketch, "E81", {"center": v(-1375, -830) * mm, "radius": 6.5 * mm});
            skCircle(sketch, "E82", {"center": v(-1375, -10) * mm, "radius": 6.5 * mm});
            skSolve(sketch);
        }
        {
            var Q0;
            Q0=makeQuery(id+"F65.imprint","IMPRINT",FACE,{"disambiguationData":[TD([[makeQuery(id+"F65.imprint","IMPRINT",EDGE,{"derivedFrom":sQuery(id+"F65.wireOp",EDGE,"E81")}),1.0]])]});
            var Q1;
            Q1=makeQuery(id+"F65.imprint","IMPRINT",FACE,{"disambiguationData":[TD([[makeQuery(id+"F65.imprint","IMPRINT",EDGE,{"derivedFrom":sQuery(id+"F65.wireOp",EDGE,"E82")}),1.0]])]});
            extrude(context, id + "F66", {"entities" : qUnion([Q0, Q1]), "operationType" : NewBodyOperationType.REMOVE, "oppositeDirection" : true, "depth" : 25 * mm});
        }
        {
            var Q0;
            Q0=makeQuery(id+"F21.opExtrude","SWEPT_FACE",FACE,{"disambiguationData":[OSD([sQuery(id+"F20.wireOp",EDGE,"E27.right")])]});
            var sketch = newSketch(context, id + "F67", { "sketchPlane" : qUnion([Q0])});
            skCircle(sketch, "E83", {"center": v(830, -14) * mm, "radius": 6.5 * mm});
            skCircle(sketch, "E84", {"center": v(10, -14) * mm, "radius": 6.5 * mm});
            skSolve(sketch);
        }
        {
            var Q0;
            Q0=makeQuery(id+"F67.imprint","IMPRINT",FACE,{"disambiguationData":[TD([[makeQuery(id+"F67.imprint","IMPRINT",EDGE,{"derivedFrom":sQuery(id+"F67.wireOp",EDGE,"E83")}),1.0]])]});
            var Q1;
            Q1=makeQuery(id+"F67.imprint","IMPRINT",FACE,{"disambiguationData":[TD([[makeQuery(id+"F67.imprint","IMPRINT",EDGE,{"derivedFrom":sQuery(id+"F67.wireOp",EDGE,"E84")}),1.0]])]});
            extrude(context, id + "F68", {"entities" : qUnion([Q0, Q1]), "operationType" : NewBodyOperationType.REMOVE, "oppositeDirection" : true, "depth" : 25 * mm});
        }
        {
            var Q0;
            Q0=makeQuery(id+"F9.opExtrude","SWEPT_FACE",FACE,{"disambiguationData":[OSD([sQuery(id+"F8.wireOp",EDGE,"E19.top")])]});
            var sketch = newSketch(context, id + "F69", { "sketchPlane" : qUnion([Q0])});
            skLineSegment(sketch, "E85.bottom", {"start": v(-825, -11) * mm, "end": v(-20, -11) * mm});
            skLineSegment(sketch, "E85.top", {"start": v(-825, 788.5) * mm, "end": v(-20, 788.5) * mm});
            skLineSegment(sketch, "E85.left", {"start": v(-825, -11) * mm, "end": v(-825, 788.5) * mm});
            skLineSegment(sketch, "E85.right", {"start": v(-20, -11) * mm, "end": v(-20, 788.5) * mm});
            skLineSegment(sketch, "E86", {"start": v(-825, -9.5) * mm, "end": v(-20, -9.5) * mm});
            skCircle(sketch, "E87", {"center": v(-100, 15) * mm, "radius": 6.5 * mm});
            skCircle(sketch, "E88", {"center": v(-800, 15) * mm, "radius": 6.5 * mm});
            skCircle(sketch, "E89", {"center": v(-800, 765) * mm, "radius": 6.5 * mm});
            skCircle(sketch, "E90", {"center": v(-100, 765) * mm, "radius": 6.5 * mm});
            skSolve(sketch);
        }
        {
            var Q0;
            {var subQ2=sQuery(id+"F69.wireOp",EDGE,"E85.top");Q0=makeQuery(id+"F69.imprint","IMPRINT",FACE,{"disambiguationData":[TD([[makeQuery(id+"F69.imprint","IMPRINT",EDGE,{"derivedFrom":subQ2}),-1.0]])]});}
            var Q1;
            {var subQ2=sQuery(id+"F69.wireOp",EDGE,"E86");Q1=makeQuery(id+"F69.imprint","IMPRINT",FACE,{"disambiguationData":[TD([[makeQuery(id+"F69.imprint","IMPRINT",EDGE,{"derivedFrom":subQ2}),1.0]])]});}
            extrude(context, id + "F70", {"entities" : qUnion([Q0, Q1]), "depth" : 2.5 * mm});
        }
        {
            var Q0;
            Q0=makeQuery(id+"F70.opExtrude","CAP_FACE",FACE,{"disambiguationData":[OSD([sQuery(id+"F69.wireOp",EDGE,"E85.top"),sQuery(id+"F69.wireOp",EDGE,"E85.left"),sQuery(id+"F69.wireOp",EDGE,"E85.right"),sQuery(id+"F69.wireOp",EDGE,"E86"),sQuery(id+"F69.wireOp",EDGE,"E87"),sQuery(id+"F69.wireOp",EDGE,"E88"),sQuery(id+"F69.wireOp",EDGE,"E89"),sQuery(id+"F69.wireOp",EDGE,"E90")])],"isStart":false});
            var sketch = newSketch(context, id + "F71", { "sketchPlane" : qUnion([Q0])});
            skLineSegment(sketch, "E91.bottom", {"start": v(-825, 788.5) * mm, "end": v(-20, 788.5) * mm});
            skLineSegment(sketch, "E91.top", {"start": v(-825, 786) * mm, "end": v(-20, 786) * mm});
            skLineSegment(sketch, "E91.left", {"start": v(-825, 788.5) * mm, "end": v(-825, 786) * mm});
            skLineSegment(sketch, "E91.right", {"start": v(-20, 788.5) * mm, "end": v(-20, 786) * mm});
            skLineSegment(sketch, "E92.bottom", {"start": v(-20, -9.5) * mm, "end": v(-825, -9.5) * mm});
            skLineSegment(sketch, "E92.top", {"start": v(-20, -7) * mm, "end": v(-825, -7) * mm});
            skLineSegment(sketch, "E92.left", {"start": v(-20, -9.5) * mm, "end": v(-20, -7) * mm});
            skLineSegment(sketch, "E92.right", {"start": v(-825, -9.5) * mm, "end": v(-825, -7) * mm});
            skSolve(sketch);
        }
        {
            var Q0;
            Q0=makeQuery(id+"F71.imprint","IMPRINT",FACE,{"disambiguationData":[TD([[makeQuery(id+"F71.imprint","IMPRINT",EDGE,{"derivedFrom":sQuery(id+"F71.wireOp",EDGE,"E92.bottom")}),1.0]])]});
            var Q1;
            Q1=makeQuery(id+"F71.imprint","IMPRINT",FACE,{"disambiguationData":[TD([[makeQuery(id+"F71.imprint","IMPRINT",EDGE,{"derivedFrom":sQuery(id+"F71.wireOp",EDGE,"E91.bottom")}),-1.0]])]});
            extrude(context, id + "F72", {"entities" : qUnion([Q0, Q1]), "operationType" : NewBodyOperationType.ADD, "depth" : 42 * mm});
        }
        {
            var Q0;
            Q0=makeQuery(id+"F11.opExtrude","CAP_FACE",FACE,{"disambiguationData":[OSD([sQuery(id+"F10.wireOp",EDGE,"E20.bottom"),sQuery(id+"F10.wireOp",EDGE,"E20.top"),sQuery(id+"F10.wireOp",EDGE,"E20.left"),sQuery(id+"F10.wireOp",EDGE,"E20.right")])],"isStart":true});
            var sketch = newSketch(context, id + "F73", { "sketchPlane" : qUnion([Q0])});
            skCircle(sketch, "E93", {"center": v(-750, 41) * mm, "radius": 6.5 * mm});
            skCircle(sketch, "E94", {"center": v(-700, 41) * mm, "radius": 6.5 * mm});
            skCircle(sketch, "E95", {"center": v(-150, 41) * mm, "radius": 6.5 * mm});
            skSolve(sketch);
        }
        {
            var Q0;
            Q0=qSketchRegion(id+"F73",true);
            extrude(context, id + "F74", {"entities" : qUnion([Q0]), "operationType" : NewBodyOperationType.REMOVE, "endBound" : BoundingType.THROUGH_ALL, "oppositeDirection" : true, "depth" : 25 * mm, "hasSecondDirection" : true, "secondDirectionBound" : SecondDirectionBoundingType.THROUGH_ALL, "secondDirectionOppositeDirection" : false, "secondDirectionDepth" : 25 * mm});
        }
        {
            var Q0;
            Q0=makeQuery(id+"F72.boolean.opBoolean","MERGE",FACE,{"derivedFrom":[makeQuery(id+"F70.opExtrude","SWEPT_FACE",FACE,{"disambiguationData":[OSD([sQuery(id+"F69.wireOp",EDGE,"E85.left")])]}),makeQuery(id+"F72.opExtrude","SWEPT_FACE",FACE,{"disambiguationData":[OSD([sQuery(id+"F71.wireOp",EDGE,"E91.left")])]}),makeQuery(id+"F72.opExtrude","SWEPT_FACE",FACE,{"disambiguationData":[OSD([sQuery(id+"F71.wireOp",EDGE,"E92.right")])]})]});
            extrude(context, id + "F75", {"entities" : qUnion([Q0]), "depth" : 870 * mm});
        }
        {
            var Q0;
            Q0=makeQuery(id+"F72.boolean.opBoolean","MERGE",FACE,{"derivedFrom":[makeQuery(id+"F70.opExtrude","SWEPT_FACE",FACE,{"disambiguationData":[OSD([sQuery(id+"F69.wireOp",EDGE,"E86")])]}),makeQuery(id+"F72.opExtrude","SWEPT_FACE",FACE,{"disambiguationData":[OSD([sQuery(id+"F71.wireOp",EDGE,"E92.bottom")])]})]});
            var sketch = newSketch(context, id + "F76", { "sketchPlane" : qUnion([Q0])});
            skCircle(sketch, "E96", {"center": v(-750, 41) * mm, "radius": 3.18 * mm});
            skCircle(sketch, "E97", {"center": v(-950, 41) * mm, "radius": 6.5 * mm});
            skCircle(sketch, "E98", {"center": v(-900, 41) * mm, "radius": 6.5 * mm});
            skCircle(sketch, "E99", {"center": v(-1570, 41) * mm, "radius": 6.5 * mm});
            skCircle(sketch, "E100", {"center": v(-1620, 41) * mm, "radius": 6.5 * mm});
            skSolve(sketch);
        }
        {
            var Q0;
            Q0=qSketchRegion(id+"F76",true);
            extrude(context, id + "F77", {"entities" : qUnion([Q0]), "operationType" : NewBodyOperationType.REMOVE, "endBound" : BoundingType.THROUGH_ALL, "oppositeDirection" : true, "depth" : 25 * mm});
        }
        {
            var Q0;
            Q0=makeQuery(id+"F70.opExtrude","CAP_FACE",FACE,{"disambiguationData":[OSD([sQuery(id+"F69.wireOp",EDGE,"E85.top"),sQuery(id+"F69.wireOp",EDGE,"E85.left"),sQuery(id+"F69.wireOp",EDGE,"E85.right"),sQuery(id+"F69.wireOp",EDGE,"E86"),sQuery(id+"F69.wireOp",EDGE,"E87"),sQuery(id+"F69.wireOp",EDGE,"E88"),sQuery(id+"F69.wireOp",EDGE,"E89"),sQuery(id+"F69.wireOp",EDGE,"E90")])],"isStart":false});
            var sketch = newSketch(context, id + "F78", { "sketchPlane" : qUnion([Q0])});
            skCircle(sketch, "E101", {"center": v(-800, 765) * mm, "radius": 4.65 * mm});
            skCircle(sketch, "E102", {"center": v(-850, 765) * mm, "radius": 6.5 * mm});
            skCircle(sketch, "E103", {"center": v(-1670, 765) * mm, "radius": 6.5 * mm});
            skCircle(sketch, "E104", {"center": v(-800, 15) * mm, "radius": 3.65 * mm});
            skCircle(sketch, "E105", {"center": v(-850, 15) * mm, "radius": 6.5 * mm});
            skCircle(sketch, "E106", {"center": v(-1670, 15) * mm, "radius": 6.5 * mm});
            skSolve(sketch);
        }
        {
            var Q0;
            Q0=qSketchRegion(id+"F78",true);
            extrude(context, id + "F79", {"entities" : qUnion([Q0]), "operationType" : NewBodyOperationType.REMOVE, "oppositeDirection" : true, "depth" : 25 * mm});
        }
        {
            var Q0;
            Q0=makeQuery(id+"F75.opExtrude","SWEPT_BODY",BODY,{"disambiguationData":[OSD([sQuery(id+"F69.wireOp",EDGE,"E85.left"),sQuery(id+"F71.wireOp",EDGE,"E91.left"),sQuery(id+"F71.wireOp",EDGE,"E92.right")])]});
            transform(context, id + "F80", {"entities" : qUnion([Q0]), "transformType" : TransformType.TRANSLATION_3D, "dx" : -870 * mm, "dy" : 0 * mm, "dz" : 0 * mm, "makeCopy" : true});
        }
        {
            var Q0;
            Q0=makeQuery(id+"F80.opPattern","COPY",FACE,{"derivedFrom":makeQuery(id+"F75.opExtrude","SWEPT_FACE",FACE,{"disambiguationData":[OSD([sQuery(id+"F69.wireOp",EDGE,"E85.left"),sQuery(id+"F69.wireOp",EDGE,"E86"),sQuery(id+"F71.wireOp",EDGE,"E92.bottom"),sQuery(id+"F71.wireOp",EDGE,"E92.right")])]}),"instanceName":"1"});
            var sketch = newSketch(context, id + "F81", { "sketchPlane" : qUnion([Q0])});
            skCircle(sketch, "E107", {"center": v(-2490, 41) * mm, "radius": 6.5 * mm});
            skCircle(sketch, "E108", {"center": v(-2440, 41) * mm, "radius": 6.5 * mm});
            skLineSegment(sketch, "E109", {"start": v(-2515.5, 64.5) * mm, "end": v(-2565, 64.5) * mm});
            skLineSegment(sketch, "E110", {"start": v(-2565, 64.5) * mm, "end": v(-2565, 20) * mm});
            skLineSegment(sketch, "E111", {"start": v(-2515.5, 64.5) * mm, "end": v(-2560, 20) * mm});
            skLineSegment(sketch, "E112", {"start": v(-2560, 20) * mm, "end": v(-2565, 20) * mm});
            skSolve(sketch);
        }
        {
            var Q0;
            Q0=makeQuery(id+"F81.imprint","IMPRINT",FACE,{"disambiguationData":[TD([[makeQuery(id+"F81.imprint","IMPRINT",EDGE,{"derivedFrom":sQuery(id+"F81.wireOp",EDGE,"E109")}),-1.0]])]});
            extrude(context, id + "F82", {"entities" : qUnion([Q0]), "operationType" : NewBodyOperationType.REMOVE, "endBound" : BoundingType.THROUGH_ALL, "oppositeDirection" : true, "depth" : 25 * mm});
        }
        {
            var Q0;
            Q0=makeQuery(id+"F81.imprint","IMPRINT",FACE,{"disambiguationData":[TD([[makeQuery(id+"F81.imprint","IMPRINT",EDGE,{"derivedFrom":sQuery(id+"F81.wireOp",EDGE,"E107")}),1.0]])]});
            var Q1;
            Q1=makeQuery(id+"F81.imprint","IMPRINT",FACE,{"disambiguationData":[TD([[makeQuery(id+"F81.imprint","IMPRINT",EDGE,{"derivedFrom":sQuery(id+"F81.wireOp",EDGE,"E108")}),1.0]])]});
            extrude(context, id + "F83", {"entities" : qUnion([Q0, Q1]), "operationType" : NewBodyOperationType.ADD, "oppositeDirection" : true, "depth" : 2.5 * mm});
        }
        {
            var Q0;
            Q0=makeQuery(id+"F80.opPattern","COPY",FACE,{"derivedFrom":makeQuery(id+"F75.opExtrude","SWEPT_FACE",FACE,{"disambiguationData":[OSD([sQuery(id+"F69.wireOp",EDGE,"E85.left"),sQuery(id+"F71.wireOp",EDGE,"E91.top"),sQuery(id+"F71.wireOp",EDGE,"E91.left")])]}),"instanceName":"1"});
            var sketch = newSketch(context, id + "F84", { "sketchPlane" : qUnion([Q0])});
            skCircle(sketch, "E113", {"center": v(-2490, 41) * mm, "radius": 6.5 * mm});
            skCircle(sketch, "E114", {"center": v(-2440, 41) * mm, "radius": 6.5 * mm});
            skSolve(sketch);
        }
        {
            var Q0;
            Q0=qSketchRegion(id+"F84",true);
            extrude(context, id + "F85", {"entities" : qUnion([Q0]), "operationType" : NewBodyOperationType.ADD, "oppositeDirection" : true, "depth" : 2.5 * mm});
        }
    });
